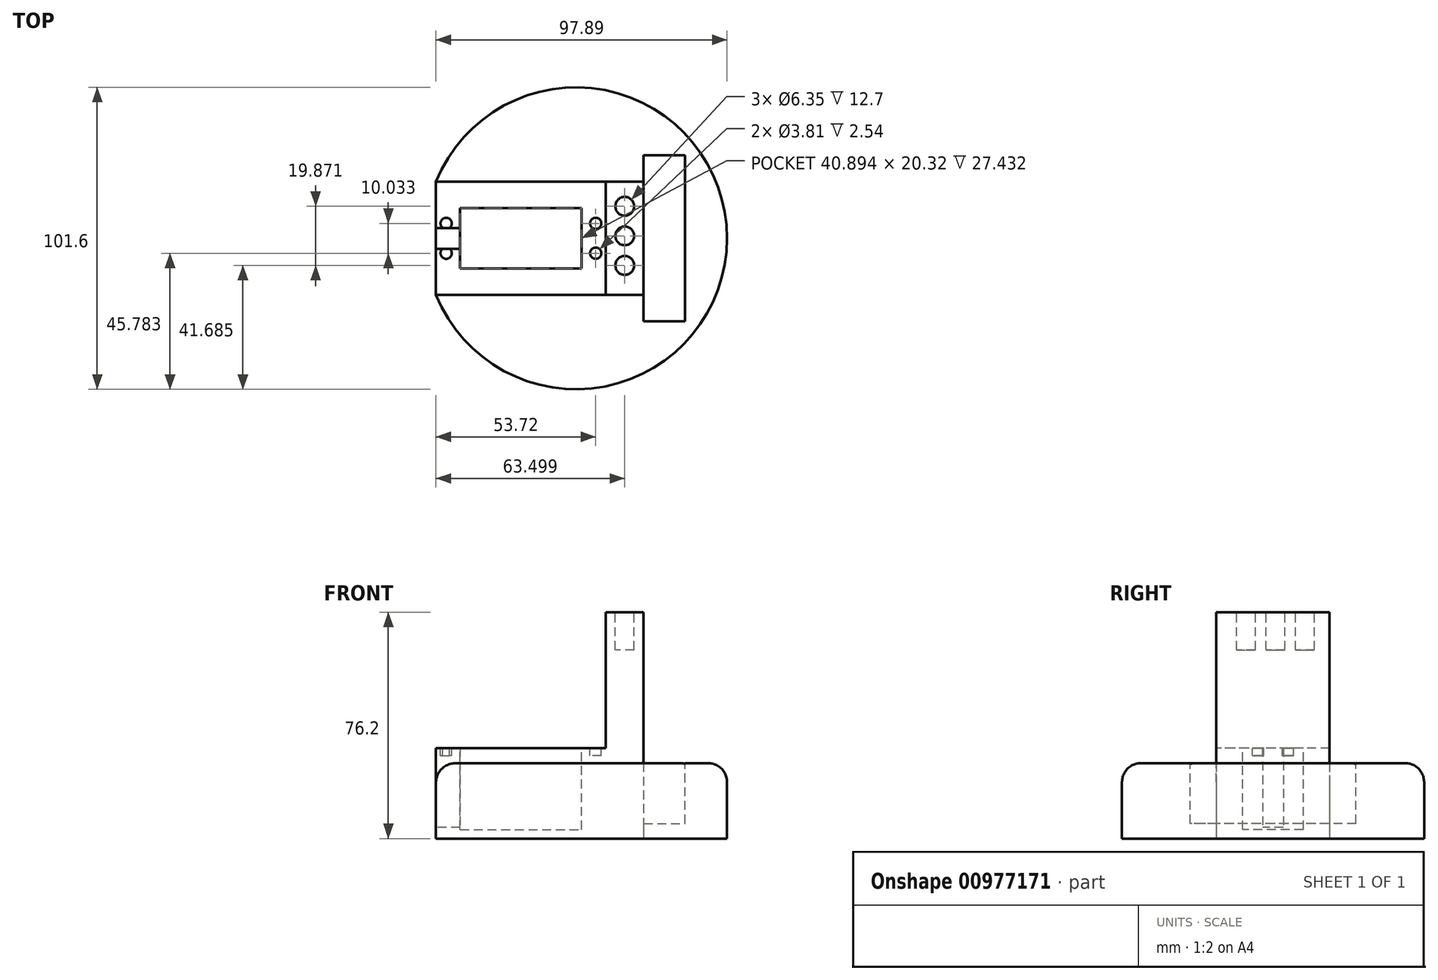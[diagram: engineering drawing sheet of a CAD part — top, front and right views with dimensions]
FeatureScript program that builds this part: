
annotation { "Feature Type Name" : "Feature", "Feature Type Description" : "" }
export const myFeature = defineFeature(function(context is Context, id is Id, definition is map)
    precondition{}
    {
        {
            var Q0;
            Q0=qCreatedBy(makeId("Top.planeOp"),FACE);
            var sketch = newSketch(context, id + "F0", { "sketchPlane" : qUnion([Q0])});
            skLineSegment(sketch, "E0.bottom", {"start": v(-19.36, 9.8) * mm, "end": v(21.1, 9.8) * mm, "construction": true});
            skLineSegment(sketch, "E0.top", {"start": v(-19.36, -10.1) * mm, "end": v(21.1, -10.1) * mm, "construction": true});
            skLineSegment(sketch, "E0.left", {"start": v(-19.36, 9.8) * mm, "end": v(-19.36, -10.1) * mm, "construction": true});
            skLineSegment(sketch, "E0.right", {"start": v(21.1, 9.8) * mm, "end": v(21.1, -10.1) * mm, "construction": true});
            skLineSegment(sketch, "E1.bottom", {"start": v(-24.2, 18.23) * mm, "end": v(32.95, 18.23) * mm});
            skLineSegment(sketch, "E1.top", {"start": v(-24.2, -19.87) * mm, "end": v(32.95, -19.87) * mm});
            skLineSegment(sketch, "E1.left", {"start": v(-24.2, 18.23) * mm, "end": v(-24.2, -19.87) * mm});
            skLineSegment(sketch, "E1.right", {"start": v(32.95, 18.23) * mm, "end": v(32.95, -19.87) * mm});
            skSolve(sketch);
        }
        {
            var Q0;
            Q0 = qSketchRegion(id + "F0", true);
            extrude(context, id + "F1", {"entities" : qUnion([Q0]), "depth" : 30.48 * mm, "offsetDistance" : 25.4 * mm});
        }
        {
            var Q0;
            Q0=makeQuery(id+"F1.opExtrude","CAP_FACE",FACE,{"disambiguationData":[OSD([sQuery(id+"F0.wireOp",EDGE,"E1.bottom"),sQuery(id+"F0.wireOp",EDGE,"E1.top"),sQuery(id+"F0.wireOp",EDGE,"E1.left"),sQuery(id+"F0.wireOp",EDGE,"E1.right")])],"isStart":false});
            var sketch = newSketch(context, id + "F2", { "sketchPlane" : qUnion([Q0])});
            skLineSegment(sketch, "E2.bottom", {"start": v(-24.2, 18.23) * mm, "end": v(32.95, 18.23) * mm, "construction": true});
            skLineSegment(sketch, "E2.top", {"start": v(-24.2, -19.87) * mm, "end": v(32.95, -19.87) * mm, "construction": true});
            skLineSegment(sketch, "E2.left", {"start": v(-24.2, 18.23) * mm, "end": v(-24.2, -19.87) * mm, "construction": true});
            skLineSegment(sketch, "E2.right", {"start": v(32.95, 18.23) * mm, "end": v(32.95, -19.87) * mm, "construction": true});
            skLineSegment(sketch, "E3.bottom", {"start": v(-16.07, 9.34) * mm, "end": v(24.82, 9.34) * mm});
            skLineSegment(sketch, "E3.top", {"start": v(-16.07, -10.98) * mm, "end": v(24.82, -10.98) * mm});
            skLineSegment(sketch, "E3.left", {"start": v(-16.07, 9.34) * mm, "end": v(-16.07, -10.98) * mm});
            skLineSegment(sketch, "E3.right", {"start": v(24.82, 9.34) * mm, "end": v(24.82, -10.98) * mm});
            skSolve(sketch);
        }
        {
            var Q0;
            Q0 = qSketchRegion(id + "F2", true);
            extrude(context, id + "F3", {"entities" : qUnion([Q0]), "operationType" : NewBodyOperationType.REMOVE, "oppositeDirection" : true, "depth" : 27.43 * mm, "offsetDistance" : 25.4 * mm});
        }
        {
            var Q0;
            Q0=qCreatedBy(makeId("Top.planeOp"),FACE);
            var sketch = newSketch(context, id + "F4", { "sketchPlane" : qUnion([Q0])});
            skLineSegment(sketch, "E4.bottom", {"start": v(32.95, 18.23) * mm, "end": v(45.65, 18.23) * mm});
            skLineSegment(sketch, "E4.top", {"start": v(32.95, -19.87) * mm, "end": v(45.65, -19.87) * mm});
            skLineSegment(sketch, "E4.left", {"start": v(32.95, 18.23) * mm, "end": v(32.95, -19.87) * mm});
            skLineSegment(sketch, "E4.right", {"start": v(45.65, 18.23) * mm, "end": v(45.65, -19.87) * mm});
            skSolve(sketch);
        }
        {
            var Q0;
            Q0 = qSketchRegion(id + "F4", true);
            extrude(context, id + "F5", {"entities" : qUnion([Q0]), "operationType" : NewBodyOperationType.ADD, "depth" : 50.8 * mm, "offsetDistance" : 25.4 * mm});
        }
        {
            var Q0;
            Q0=makeQuery(id+"F1.opExtrude","SWEPT_FACE",FACE,{"disambiguationData":[OSD([sQuery(id+"F0.wireOp",EDGE,"E1.left")])]});
            var sketch = newSketch(context, id + "F6", { "sketchPlane" : qUnion([Q0])});
            skLineSegment(sketch, "E5.bottom", {"start": v(-2.67, 30.48) * mm, "end": v(4.31, 30.48) * mm});
            skLineSegment(sketch, "E5.top", {"start": v(-2.67, 3.81) * mm, "end": v(4.31, 3.81) * mm});
            skLineSegment(sketch, "E5.left", {"start": v(-2.67, 30.48) * mm, "end": v(-2.67, 3.81) * mm});
            skLineSegment(sketch, "E5.right", {"start": v(4.31, 30.48) * mm, "end": v(4.31, 3.81) * mm});
            skSolve(sketch);
        }
        {
            var Q0;
            Q0 = qSketchRegion(id + "F6", true);
            extrude(context, id + "F7", {"entities" : qUnion([Q0]), "operationType" : NewBodyOperationType.REMOVE, "oppositeDirection" : true, "depth" : 12.95 * mm, "offsetDistance" : 25.4 * mm});
        }
        {
            var Q0;
            Q0=makeQuery(id+"F1.opExtrude","CAP_FACE",FACE,{"disambiguationData":[OSD([sQuery(id+"F0.wireOp",EDGE,"E1.bottom"),sQuery(id+"F0.wireOp",EDGE,"E1.top"),sQuery(id+"F0.wireOp",EDGE,"E1.left"),sQuery(id+"F0.wireOp",EDGE,"E1.right")])],"isStart":false});
            var sketch = newSketch(context, id + "F8", { "sketchPlane" : qUnion([Q0])});
            skLineSegment(sketch, "E6", {"start": v(-20.77, 2.3) * mm, "end": v(-20.77, -3.93) * mm, "construction": true});
            skCircle(sketch, "E7", {"center": v(-20.77, 4.2) * mm, "radius": 1.9 * mm});
            skCircle(sketch, "E8", {"center": v(-20.77, -5.84) * mm, "radius": 1.9 * mm});
            skLineSegment(sketch, "E9", {"start": v(29.52, 2.3) * mm, "end": v(29.52, -3.93) * mm, "construction": true});
            skCircle(sketch, "E10", {"center": v(29.52, 4.2) * mm, "radius": 1.9 * mm});
            skCircle(sketch, "E11", {"center": v(29.52, -5.84) * mm, "radius": 1.9 * mm});
            skSolve(sketch);
        }
        {
            var Q0;
            Q0 = qSketchRegion(id + "F8", true);
            extrude(context, id + "F9", {"entities" : qUnion([Q0]), "operationType" : NewBodyOperationType.REMOVE, "oppositeDirection" : true, "depth" : 2.54 * mm, "offsetDistance" : 25.4 * mm});
        }
        {
            var Q0;
            Q0=qCreatedBy(makeId("Top.planeOp"),FACE);
            var sketch = newSketch(context, id + "F10", { "sketchPlane" : qUnion([Q0])});
            skLineSegment(sketch, "E12", {"start": v(-24.2, 18.23) * mm, "end": v(45.65, 18.23) * mm});
            skLineSegment(sketch, "E13", {"start": v(45.65, 18.23) * mm, "end": v(45.65, -19.87) * mm});
            skLineSegment(sketch, "E14", {"start": v(45.65, -19.87) * mm, "end": v(-24.2, -19.87) * mm});
            skArc(sketch, "E15", {"start": v(-24.2, -19.87) * mm, "mid": v(73.7, -0.82) * mm, "end": v(-24.2, 18.23) * mm});
            skSolve(sketch);
        }
        {
            var Q0;
            Q0 = qSketchRegion(id + "F10", true);
            extrude(context, id + "F11", {"entities" : qUnion([Q0]), "depth" : 25.4 * mm, "offsetDistance" : 25.4 * mm});
        }
        {
            var Q0;
            Q0=makeQuery(id+"F11.opExtrude","CAP_FACE",FACE,{"disambiguationData":[OSD([sQuery(id+"F10.wireOp",EDGE,"Zpmwydhr-uNuY-9Eg6-auXW-bJKq4jWZyT8T"),sQuery(id+"F10.wireOp",EDGE,"E12"),sQuery(id+"F10.wireOp",EDGE,"E13"),sQuery(id+"F10.wireOp",EDGE,"E14")])],"isStart":false});
            var sketch = newSketch(context, id + "F12", { "sketchPlane" : qUnion([Q0])});
            skLineSegment(sketch, "E16.bottom", {"start": v(45.65, 27.12) * mm, "end": v(59.62, 27.12) * mm});
            skLineSegment(sketch, "E16.top", {"start": v(45.65, -28.76) * mm, "end": v(59.62, -28.76) * mm});
            skLineSegment(sketch, "E16.left", {"start": v(45.65, 27.12) * mm, "end": v(45.65, -28.76) * mm});
            skLineSegment(sketch, "E16.right", {"start": v(59.62, 27.12) * mm, "end": v(59.62, -28.76) * mm});
            skSolve(sketch);
        }
        {
            var Q0;
            Q0 = qSketchRegion(id + "F12", true);
            extrude(context, id + "F13", {"entities" : qUnion([Q0]), "operationType" : NewBodyOperationType.REMOVE, "oppositeDirection" : true, "depth" : 20.32 * mm, "offsetDistance" : 25.4 * mm});
        }
        {
            var Q0;
            Q0=makeQuery(id+"F11.opExtrude","CAP_EDGE",EDGE,{"disambiguationData":[OSD([sQuery(id+"F10.wireOp",EDGE,"E15")])],"isStart":false});
            fillet(context, id + "F14", {"entities" : qUnion([Q0]), "radius" : 6.35 * mm, "tangentPropagation" : true, "allowEdgeOverflow" : false});
        }
        {
            var Q0;
            Q0=makeQuery(id+"F5.opExtrude","CAP_FACE",FACE,{"disambiguationData":[OSD([sQuery(id+"F4.wireOp",EDGE,"E4.bottom"),sQuery(id+"F4.wireOp",EDGE,"E4.top"),sQuery(id+"F4.wireOp",EDGE,"E4.left"),sQuery(id+"F4.wireOp",EDGE,"E4.right")])],"isStart":false});
            extrude(context, id + "F15", {"entities" : qUnion([Q0]), "operationType" : NewBodyOperationType.ADD, "depth" : 25.4 * mm, "offsetDistance" : 25.4 * mm});
        }
        {
            var Q0;
            Q0=makeQuery(id+"F15.opExtrude","CAP_FACE",FACE,{"disambiguationData":[OSD([sQuery(id+"F4.wireOp",EDGE,"E4.bottom"),sQuery(id+"F4.wireOp",EDGE,"E4.top"),sQuery(id+"F4.wireOp",EDGE,"E4.left"),sQuery(id+"F4.wireOp",EDGE,"E4.right")])],"isStart":false});
            var sketch = newSketch(context, id + "F16", { "sketchPlane" : qUnion([Q0])});
            skCircle(sketch, "E17", {"center": v(39.3, 9.94) * mm, "radius": 3.18 * mm});
            skPoint(sketch, "E17.centerSnap0", {"position": v(39.3, 18.23) * mm});
            skCircle(sketch, "E18", {"center": v(39.3, 0) * mm, "radius": 3.18 * mm});
            skCircle(sketch, "E19", {"center": v(39.3, -9.94) * mm, "radius": 3.18 * mm});
            skSolve(sketch);
        }
        {
            var Q0;
            Q0 = qSketchRegion(id + "F16", true);
            extrude(context, id + "F17", {"entities" : qUnion([Q0]), "operationType" : NewBodyOperationType.REMOVE, "oppositeDirection" : true, "depth" : 12.7 * mm, "offsetDistance" : 25.4 * mm});
        }
        {
            var Q0;
            Q0=makeQuery(id+"F1.opExtrude","SWEPT_BODY",BODY,{"disambiguationData":[OSD([sQuery(id+"F0.wireOp",EDGE,"E1.bottom"),sQuery(id+"F0.wireOp",EDGE,"E1.top"),sQuery(id+"F0.wireOp",EDGE,"E1.left"),sQuery(id+"F0.wireOp",EDGE,"E1.right")])]});
            transform(context, id + "F18", {"entities" : qUnion([Q0]), "transformType" : TransformType.TRANSLATION_3D, "dx" : 0 * mm, "dy" : -119.13 * mm, "dz" : 0 * mm, "makeCopy" : true});
        }
        {
            var Q0;
            Q0=makeQuery(id+"F18.opPattern","COPY",BODY,{"derivedFrom":makeQuery(id+"F1.opExtrude","SWEPT_BODY",BODY,{"disambiguationData":[OSD([sQuery(id+"F0.wireOp",EDGE,"E1.bottom"),sQuery(id+"F0.wireOp",EDGE,"E1.top"),sQuery(id+"F0.wireOp",EDGE,"E1.left"),sQuery(id+"F0.wireOp",EDGE,"E1.right")])]}),"instanceName":"1"});
            deleteBodies(context, id + "F19", {"entities" : qUnion([Q0])});
        }
    });
